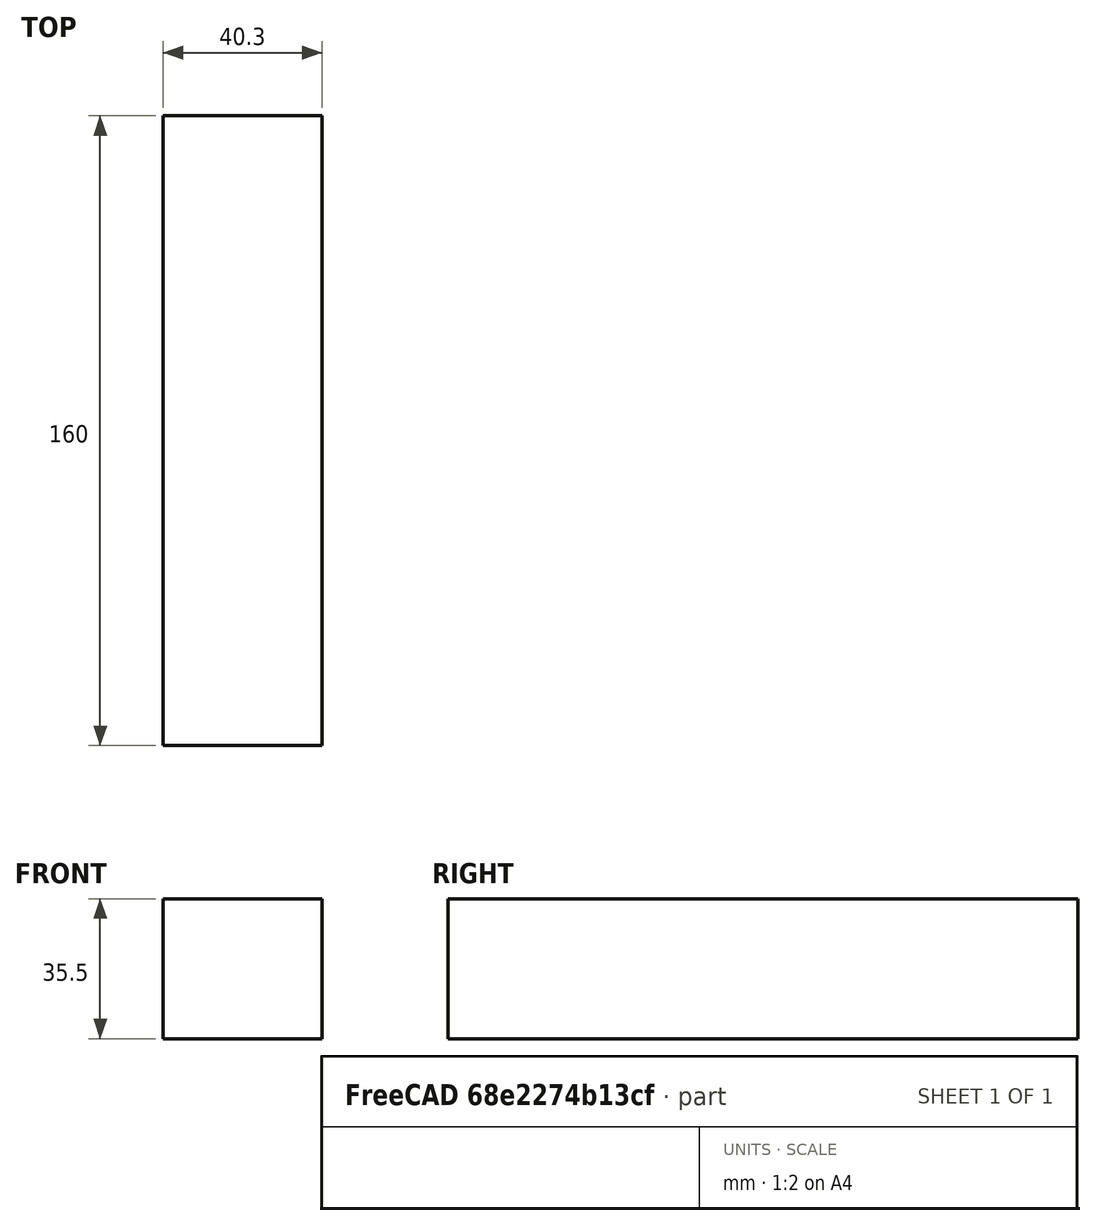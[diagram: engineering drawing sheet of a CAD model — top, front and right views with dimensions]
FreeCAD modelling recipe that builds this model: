
FCSTD DOCUMENT  (FreeCAD 1.1R38827 (Git))
Label: UET-VAS-060A20_12V_IP20
License: All rights reserved
LicenseURL: http://en.wikipedia.org/wiki/All_rights_reserved
objects: PartDesign::AdditiveBox×1, PartDesign::Body×1, Sketcher::SketchObject×1
note: 6 computed .brp shape members not serialized (recipe doc carries the construction recipe); baked Part::Feature solids carry a one-line shape summary decoded from their .brp

FEATURE [PartDesign::AdditiveBox] Box
  AttacherType = Attacher::AttachEngine3D
  AttachmentOffset = pos=(-20.15,-80,0) rot=(0,0,1;0rad)
  AttachmentSupport = -> [XY_Plane]
  Height = 35.5
  Length = 40.3
  MapMode = 5
  Placement = pos=(-20.15,-80,0) rot=(0,0,1;0rad)
  Suppressed = false
  Width = 160
  expr: .AttachmentOffset.Base.x = -Length / 2
  expr: .AttachmentOffset.Base.y = -Width / 2
FEATURE [PartDesign::Body] Body
  AllowCompound = false
  Group = -> [Box]
  Origin = -> Origin
  Tip = -> Box
FEATURE [Sketcher::SketchObject] Sketch001  label="holes"
  ArcFitTolerance = 0
  FullyConstrained = true
  MakeInternals = false
  sketch-geometry (2):
    g0: Circle CenterX=13.2 CenterY=-75.0683 CenterZ=0 NormalX=0 NormalY=0 NormalZ=1 AngleXU=0 Radius=1.7
    g1: Circle CenterX=-13.2 CenterY=75.0683 CenterZ=0 NormalX=0 NormalY=0 NormalZ=1 AngleXU=0 Radius=1.7
  constraints (5):
    c: Symmetric(g1,g0,g-1)
    c: Distance(g0,g1) = 152.44
    c: Equal(g0,g1)
    c: Diameter(g0) = 3.4
    c: DistanceX(g1) = -13.2
